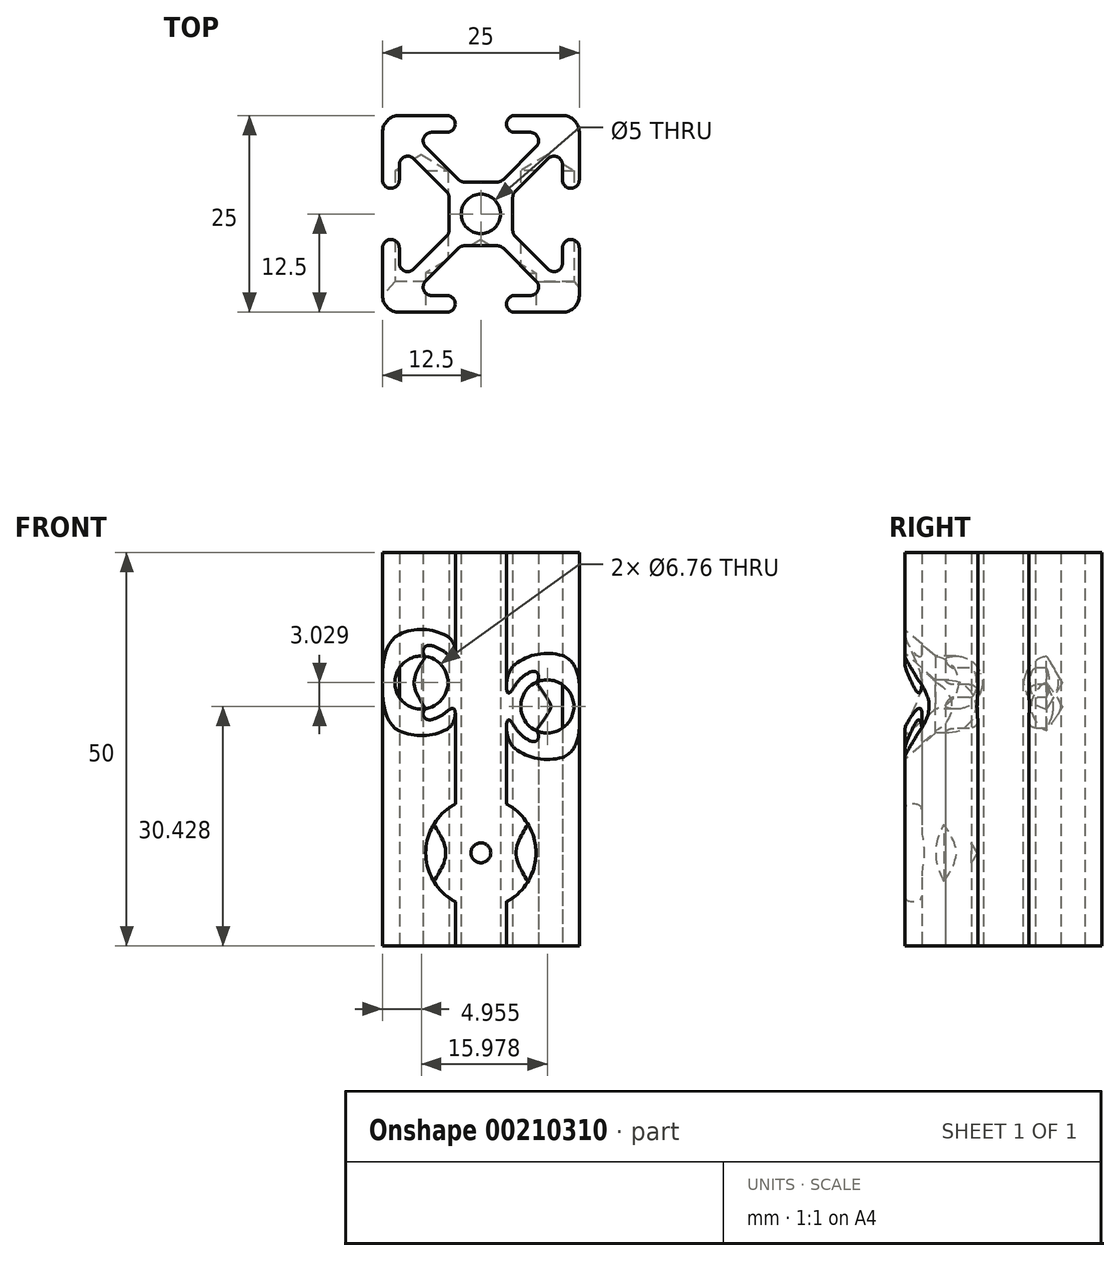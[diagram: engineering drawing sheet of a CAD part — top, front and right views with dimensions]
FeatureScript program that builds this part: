
annotation { "Feature Type Name" : "Feature", "Feature Type Description" : "" }
export const myFeature = defineFeature(function(context is Context, id is Id, definition is map)
    precondition{}
    {
        {
            var Q0;
            Q0=qCreatedBy(makeId("Top.planeOp"),FACE);
            var sketch = newSketch(context, id + "F0", { "sketchPlane" : qUnion([Q0])});
            skCircle(sketch, "E0", {"center": v(0, 0) * mm, "radius": 2.5 * mm});
            skLineSegment(sketch, "E1", {"start": v(0, 0) * mm, "end": v(0, 4.05) * mm, "construction": true});
            skLineSegment(sketch, "E2", {"start": v(0, 0) * mm, "end": v(-4.05, 0) * mm, "construction": true});
            skLineSegment(sketch, "E3", {"start": v(0, 0) * mm, "end": v(-12.5, 12.5) * mm, "construction": true});
            skLineSegment(sketch, "E4", {"start": v(-12.5, 10.36) * mm, "end": v(-12.5, 4.32) * mm});
            skLineSegment(sketch, "E5", {"start": v(-10.36, 12.5) * mm, "end": v(-4.32, 12.5) * mm});
            skLineSegment(sketch, "E6", {"start": v(-4.32, 10.36) * mm, "end": v(-6.26, 10.36) * mm});
            skLineSegment(sketch, "E7", {"start": v(-10.36, 6.26) * mm, "end": v(-10.36, 4.32) * mm});
            skArc(sketch, "E8", {"start": v(-4.32, 12.5) * mm, "mid": v(-3.25, 11.43) * mm, "end": v(-4.32, 10.36) * mm});
            skArc(sketch, "E9", {"start": v(-10.36, 4.32) * mm, "mid": v(-11.43, 3.25) * mm, "end": v(-12.5, 4.32) * mm});
            skLineSegment(sketch, "E10", {"start": v(0, 4.05) * mm, "end": v(-2.1, 4.05) * mm});
            skLineSegment(sketch, "E11", {"start": v(-4.05, 2.1) * mm, "end": v(-4.05, 0) * mm});
            skLineSegment(sketch, "E12", {"start": v(-8.53, 7.02) * mm, "end": v(-4.36, 2.85) * mm});
            skLineSegment(sketch, "E13", {"start": v(-7.02, 8.53) * mm, "end": v(-2.85, 4.36) * mm});
            skLineSegment(sketch, "E14.0.MirrorCS", {"start": v(10.36, 6.26) * mm, "end": v(10.36, 4.32) * mm});
            skLineSegment(sketch, "E14.1.MirrorCS", {"start": v(7.02, 8.53) * mm, "end": v(2.85, 4.36) * mm});
            skArc(sketch, "E14.2.MirrorCS", {"start": v(4.32, 12.5) * mm, "mid": v(3.25, 11.43) * mm, "end": v(4.32, 10.36) * mm});
            skArc(sketch, "E14.3.MirrorCS", {"start": v(10.36, 4.32) * mm, "mid": v(11.43, 3.25) * mm, "end": v(12.5, 4.32) * mm});
            skLineSegment(sketch, "E14.4.MirrorCS", {"start": v(10.36, 12.5) * mm, "end": v(4.32, 12.5) * mm});
            skLineSegment(sketch, "E14.5.MirrorCS", {"start": v(4.32, 10.36) * mm, "end": v(6.26, 10.36) * mm});
            skLineSegment(sketch, "E14.6.MirrorCS", {"start": v(12.5, 10.36) * mm, "end": v(12.5, 4.32) * mm});
            skLineSegment(sketch, "E14.7.MirrorCS", {"start": v(8.53, 7.02) * mm, "end": v(4.36, 2.85) * mm});
            skLineSegment(sketch, "E15.0.MirrorCS", {"start": v(0, 4.05) * mm, "end": v(2.1, 4.05) * mm});
            skLineSegment(sketch, "E16.0.MirrorCS", {"start": v(4.05, 2.1) * mm, "end": v(4.05, 0) * mm});
            skLineSegment(sketch, "E17.0.MirrorCS", {"start": v(10.36, -12.5) * mm, "end": v(4.32, -12.5) * mm});
            skLineSegment(sketch, "E17.1.MirrorCS", {"start": v(12.5, -10.36) * mm, "end": v(12.5, -4.32) * mm});
            skArc(sketch, "E17.2.MirrorCS", {"start": v(4.32, -12.5) * mm, "mid": v(3.25, -11.43) * mm, "end": v(4.32, -10.36) * mm});
            skLineSegment(sketch, "E17.3.MirrorCS", {"start": v(-7.02, -8.53) * mm, "end": v(-2.85, -4.36) * mm});
            skLineSegment(sketch, "E17.4.MirrorCS", {"start": v(7.02, -8.53) * mm, "end": v(2.85, -4.36) * mm});
            skLineSegment(sketch, "E17.5.MirrorCS", {"start": v(10.36, -6.26) * mm, "end": v(10.36, -4.32) * mm});
            skLineSegment(sketch, "E17.6.MirrorCS", {"start": v(8.53, -7.02) * mm, "end": v(4.36, -2.85) * mm});
            skLineSegment(sketch, "E17.7.MirrorCS", {"start": v(-10.36, -12.5) * mm, "end": v(-4.32, -12.5) * mm});
            skLineSegment(sketch, "E17.8.MirrorCS", {"start": v(-4.32, -10.36) * mm, "end": v(-6.26, -10.36) * mm});
            skLineSegment(sketch, "E17.9.MirrorCS", {"start": v(4.32, -10.36) * mm, "end": v(6.26, -10.36) * mm});
            skArc(sketch, "E17.10.MirrorCS", {"start": v(10.36, -4.32) * mm, "mid": v(11.43, -3.25) * mm, "end": v(12.5, -4.32) * mm});
            skLineSegment(sketch, "E17.11.MirrorCS", {"start": v(-12.5, -10.36) * mm, "end": v(-12.5, -4.32) * mm});
            skLineSegment(sketch, "E17.12.MirrorCS", {"start": v(0, -4.05) * mm, "end": v(2.1, -4.05) * mm});
            skArc(sketch, "E17.13.MirrorCS", {"start": v(-4.32, -12.5) * mm, "mid": v(-3.25, -11.43) * mm, "end": v(-4.32, -10.36) * mm});
            skLineSegment(sketch, "E17.14.MirrorCS", {"start": v(-8.53, -7.02) * mm, "end": v(-4.36, -2.85) * mm});
            skArc(sketch, "E17.15.MirrorCS", {"start": v(-10.36, -4.32) * mm, "mid": v(-11.43, -3.25) * mm, "end": v(-12.5, -4.32) * mm});
            skLineSegment(sketch, "E17.16.MirrorCS", {"start": v(-10.36, -6.26) * mm, "end": v(-10.36, -4.32) * mm});
            skLineSegment(sketch, "E17.17.MirrorCS", {"start": v(0, -4.05) * mm, "end": v(-2.1, -4.05) * mm});
            skLineSegment(sketch, "E18.0.MirrorCS", {"start": v(4.05, -2.1) * mm, "end": v(4.05, 0) * mm});
            skLineSegment(sketch, "E19.0.MirrorCS", {"start": v(-4.05, -2.1) * mm, "end": v(-4.05, 0) * mm});
            skPoint(sketch, "E20.visualSharp", {"position": v(-12.5, 12.5) * mm});
            skArc(sketch, "E20.filletArc", {"start": v(-10.36, 12.5) * mm, "mid": v(-11.87, 11.87) * mm, "end": v(-12.5, 10.36) * mm});
            skPoint(sketch, "E21.visualSharp", {"position": v(12.5, 12.5) * mm});
            skArc(sketch, "E21.filletArc", {"start": v(12.5, 10.36) * mm, "mid": v(11.87, 11.87) * mm, "end": v(10.36, 12.5) * mm});
            skPoint(sketch, "E22.visualSharp", {"position": v(12.5, -12.5) * mm});
            skArc(sketch, "E22.filletArc", {"start": v(10.36, -12.5) * mm, "mid": v(11.87, -11.87) * mm, "end": v(12.5, -10.36) * mm});
            skPoint(sketch, "E23.visualSharp", {"position": v(-12.5, -12.5) * mm});
            skArc(sketch, "E23.filletArc", {"start": v(-12.5, -10.36) * mm, "mid": v(-11.87, -11.87) * mm, "end": v(-10.36, -12.5) * mm});
            skPoint(sketch, "E24.visualSharp", {"position": v(4.05, 4.05) * mm});
            skPoint(sketch, "E25.visualSharp", {"position": v(-10.36, 8.85) * mm});
            skArc(sketch, "E25.filletArc", {"start": v(-8.53, 7.02) * mm, "mid": v(-9.7, 7.25) * mm, "end": v(-10.36, 6.26) * mm});
            skPoint(sketch, "E26.visualSharp", {"position": v(-8.85, 10.36) * mm});
            skArc(sketch, "E26.filletArc", {"start": v(-6.26, 10.36) * mm, "mid": v(-7.25, 9.7) * mm, "end": v(-7.02, 8.53) * mm});
            skPoint(sketch, "E27.visualSharp", {"position": v(8.85, 10.36) * mm});
            skArc(sketch, "E27.filletArc", {"start": v(7.02, 8.53) * mm, "mid": v(7.25, 9.7) * mm, "end": v(6.26, 10.36) * mm});
            skPoint(sketch, "E28.visualSharp", {"position": v(10.36, 8.85) * mm});
            skArc(sketch, "E28.filletArc", {"start": v(10.36, 6.26) * mm, "mid": v(9.7, 7.25) * mm, "end": v(8.53, 7.02) * mm});
            skPoint(sketch, "E29.visualSharp", {"position": v(10.36, -8.85) * mm});
            skArc(sketch, "E29.filletArc", {"start": v(8.53, -7.02) * mm, "mid": v(9.7, -7.25) * mm, "end": v(10.36, -6.26) * mm});
            skPoint(sketch, "E30.visualSharp", {"position": v(8.85, -10.36) * mm});
            skArc(sketch, "E30.filletArc", {"start": v(6.26, -10.36) * mm, "mid": v(7.25, -9.7) * mm, "end": v(7.02, -8.53) * mm});
            skPoint(sketch, "E31.visualSharp", {"position": v(-8.85, -10.36) * mm});
            skArc(sketch, "E31.filletArc", {"start": v(-7.02, -8.53) * mm, "mid": v(-7.25, -9.7) * mm, "end": v(-6.26, -10.36) * mm});
            skPoint(sketch, "E32.visualSharp", {"position": v(-10.36, -8.85) * mm});
            skArc(sketch, "E32.filletArc", {"start": v(-10.36, -6.26) * mm, "mid": v(-9.7, -7.25) * mm, "end": v(-8.53, -7.02) * mm});
            skPoint(sketch, "E33.orphan", {"position": v(-4.05, 4.05) * mm});
            skPoint(sketch, "E34.orphan", {"position": v(4.05, -4.05) * mm});
            skPoint(sketch, "E35.orphan", {"position": v(-4.05, -4.05) * mm});
            skPoint(sketch, "E36.visualSharp", {"position": v(-2.54, 4.05) * mm});
            skArc(sketch, "E36.filletArc", {"start": v(-2.85, 4.36) * mm, "mid": v(-2.5, 4.13) * mm, "end": v(-2.1, 4.05) * mm});
            skPoint(sketch, "E37.visualSharp", {"position": v(2.54, 4.05) * mm});
            skArc(sketch, "E37.filletArc", {"start": v(2.1, 4.05) * mm, "mid": v(2.5, 4.13) * mm, "end": v(2.85, 4.36) * mm});
            skPoint(sketch, "E38.visualSharp", {"position": v(-4.05, 2.54) * mm});
            skArc(sketch, "E38.filletArc", {"start": v(-4.05, 2.1) * mm, "mid": v(-4.13, 2.5) * mm, "end": v(-4.36, 2.85) * mm});
            skPoint(sketch, "E39.visualSharp", {"position": v(-4.05, -2.54) * mm});
            skArc(sketch, "E39.filletArc", {"start": v(-4.36, -2.85) * mm, "mid": v(-4.13, -2.5) * mm, "end": v(-4.05, -2.1) * mm});
            skPoint(sketch, "E40.visualSharp", {"position": v(-2.54, -4.05) * mm});
            skArc(sketch, "E40.filletArc", {"start": v(-2.1, -4.05) * mm, "mid": v(-2.5, -4.13) * mm, "end": v(-2.85, -4.36) * mm});
            skPoint(sketch, "E41.visualSharp", {"position": v(2.54, -4.05) * mm});
            skArc(sketch, "E41.filletArc", {"start": v(2.85, -4.36) * mm, "mid": v(2.5, -4.13) * mm, "end": v(2.1, -4.05) * mm});
            skPoint(sketch, "E42.visualSharp", {"position": v(4.05, -2.54) * mm});
            skArc(sketch, "E42.filletArc", {"start": v(4.05, -2.1) * mm, "mid": v(4.13, -2.5) * mm, "end": v(4.36, -2.85) * mm});
            skPoint(sketch, "E43.visualSharp", {"position": v(4.05, 2.54) * mm});
            skArc(sketch, "E43.filletArc", {"start": v(4.36, 2.85) * mm, "mid": v(4.13, 2.5) * mm, "end": v(4.05, 2.1) * mm});
            skSolve(sketch);
        }
        {
            var Q0;
            Q0=makeQuery(id+"F0.imprint","IMPRINT",FACE,{"disambiguationData":[TD([[makeQuery(id+"F0.imprint","IMPRINT",EDGE,{"derivedFrom":sQuery(id+"F0.wireOp",EDGE,"E0")}),-1.0]])]});
            extrude(context, id + "F1", {"entities" : qUnion([Q0]), "depth" : 50 * mm});
        }
        {
            var Q0;
            Q0=makeQuery(id+"F1.opExtrude","SWEPT_FACE",FACE,{"disambiguationData":[OSD([sQuery(id+"F0.wireOp",EDGE,"E17.7.MirrorCS")])]});
            var sketch = newSketch(context, id + "F2", { "sketchPlane" : qUnion([Q0])});
            skPoint(sketch, "E44", {"position": v(8.43, 30.43) * mm});
            skPoint(sketch, "E45", {"position": v(-7.55, 33.46) * mm});
            skSolve(sketch);
        }
        {
            var Q0;
            Q0=sQuery(id+"F2.wireOp",VERTEX,"E45");
            var Q1;
            Q1=sQuery(id+"F2.wireOp",VERTEX,"E44");
            var Q2;
            Q2=makeQuery(id+"F1.opExtrude","SWEPT_BODY",BODY,{"disambiguationData":[OSD([sQuery(id+"F0.wireOp",EDGE,"E0"),sQuery(id+"F0.wireOp",EDGE,"E4"),sQuery(id+"F0.wireOp",EDGE,"E5"),sQuery(id+"F0.wireOp",EDGE,"E6"),sQuery(id+"F0.wireOp",EDGE,"E7"),sQuery(id+"F0.wireOp",EDGE,"E8"),sQuery(id+"F0.wireOp",EDGE,"E9"),sQuery(id+"F0.wireOp",EDGE,"E11"),sQuery(id+"F0.wireOp",EDGE,"E12"),sQuery(id+"F0.wireOp",EDGE,"E13"),sQuery(id+"F0.wireOp",EDGE,"E14.0.MirrorCS"),sQuery(id+"F0.wireOp",EDGE,"E14.1.MirrorCS"),sQuery(id+"F0.wireOp",EDGE,"E14.2.MirrorCS"),sQuery(id+"F0.wireOp",EDGE,"E14.3.MirrorCS"),sQuery(id+"F0.wireOp",EDGE,"E14.4.MirrorCS"),sQuery(id+"F0.wireOp",EDGE,"E14.5.MirrorCS"),sQuery(id+"F0.wireOp",EDGE,"E14.6.MirrorCS"),sQuery(id+"F0.wireOp",EDGE,"E14.7.MirrorCS"),sQuery(id+"F0.wireOp",EDGE,"E15.0.MirrorCS"),sQuery(id+"F0.wireOp",EDGE,"E17.0.MirrorCS"),sQuery(id+"F0.wireOp",EDGE,"E17.1.MirrorCS"),sQuery(id+"F0.wireOp",EDGE,"E17.2.MirrorCS"),sQuery(id+"F0.wireOp",EDGE,"E17.3.MirrorCS"),sQuery(id+"F0.wireOp",EDGE,"E17.4.MirrorCS"),sQuery(id+"F0.wireOp",EDGE,"E17.5.MirrorCS"),sQuery(id+"F0.wireOp",EDGE,"E17.6.MirrorCS"),sQuery(id+"F0.wireOp",EDGE,"E17.7.MirrorCS"),sQuery(id+"F0.wireOp",EDGE,"E17.8.MirrorCS"),sQuery(id+"F0.wireOp",EDGE,"E17.9.MirrorCS"),sQuery(id+"F0.wireOp",EDGE,"E17.10.MirrorCS"),sQuery(id+"F0.wireOp",EDGE,"E17.11.MirrorCS"),sQuery(id+"F0.wireOp",EDGE,"E17.13.MirrorCS"),sQuery(id+"F0.wireOp",EDGE,"E17.14.MirrorCS"),sQuery(id+"F0.wireOp",EDGE,"E17.15.MirrorCS"),sQuery(id+"F0.wireOp",EDGE,"E17.16.MirrorCS"),sQuery(id+"F0.wireOp",EDGE,"E17.17.MirrorCS"),sQuery(id+"F0.wireOp",EDGE,"E18.0.MirrorCS"),sQuery(id+"F0.wireOp",EDGE,"E20.filletArc"),sQuery(id+"F0.wireOp",EDGE,"E21.filletArc"),sQuery(id+"F0.wireOp",EDGE,"E22.filletArc"),sQuery(id+"F0.wireOp",EDGE,"E23.filletArc"),sQuery(id+"F0.wireOp",EDGE,"E25.filletArc"),sQuery(id+"F0.wireOp",EDGE,"E26.filletArc"),sQuery(id+"F0.wireOp",EDGE,"E27.filletArc"),sQuery(id+"F0.wireOp",EDGE,"E28.filletArc"),sQuery(id+"F0.wireOp",EDGE,"E29.filletArc"),sQuery(id+"F0.wireOp",EDGE,"E30.filletArc"),sQuery(id+"F0.wireOp",EDGE,"E31.filletArc"),sQuery(id+"F0.wireOp",EDGE,"E32.filletArc"),sQuery(id+"F0.wireOp",EDGE,"E36.filletArc"),sQuery(id+"F0.wireOp",EDGE,"E37.filletArc"),sQuery(id+"F0.wireOp",EDGE,"E38.filletArc"),sQuery(id+"F0.wireOp",EDGE,"E39.filletArc"),sQuery(id+"F0.wireOp",EDGE,"E40.filletArc"),sQuery(id+"F0.wireOp",EDGE,"E41.filletArc"),sQuery(id+"F0.wireOp",EDGE,"E42.filletArc"),sQuery(id+"F0.wireOp",EDGE,"E43.filletArc")])]});
            hole(context, id + "F3", {"style" : HoleStyle.C_SINK, "endStyle" : HoleEndStyle.BLIND, "standardTappedOrClearance" : lookupTablePath({ "standard" : "ANSI", "fit" : "Normal (ASME)", "size" : "1/4", "type" : "Clearance" }), "standardBlindInLast" : lookupTablePath({ "fit" : "Free", "standard" : "ANSI", "size" : "1/4", "type" : "Clearance" }), "holeDiameter" : 6.76 * mm, "cSinkDiameter" : 13.5 * mm, "cSinkAngle" : 82 * degree, "holeDepth" : 18 * mm, "locations" : qUnion([Q0, Q1]), "scope" : qUnion([Q2])});
        }
        {
            var Q0;
            Q0=makeQuery(id+"F1.opExtrude","SWEPT_FACE",FACE,{"disambiguationData":[OSD([sQuery(id+"F0.wireOp",EDGE,"E17.0.MirrorCS")])]});
            var sketch = newSketch(context, id + "F4", { "sketchPlane" : qUnion([Q0])});
            skPoint(sketch, "E46", {"position": v(0, 11.83) * mm});
            skSolve(sketch);
        }
        {
            var Q0;
            Q0=sQuery(id+"F4.wireOp",VERTEX,"E46");
            var Q1;
            Q1=makeQuery(id+"F1.opExtrude","SWEPT_BODY",BODY,{"disambiguationData":[OSD([sQuery(id+"F0.wireOp",EDGE,"E0"),sQuery(id+"F0.wireOp",EDGE,"E4"),sQuery(id+"F0.wireOp",EDGE,"E5"),sQuery(id+"F0.wireOp",EDGE,"E6"),sQuery(id+"F0.wireOp",EDGE,"E7"),sQuery(id+"F0.wireOp",EDGE,"E8"),sQuery(id+"F0.wireOp",EDGE,"E9"),sQuery(id+"F0.wireOp",EDGE,"E11"),sQuery(id+"F0.wireOp",EDGE,"E12"),sQuery(id+"F0.wireOp",EDGE,"E13"),sQuery(id+"F0.wireOp",EDGE,"E14.0.MirrorCS"),sQuery(id+"F0.wireOp",EDGE,"E14.1.MirrorCS"),sQuery(id+"F0.wireOp",EDGE,"E14.2.MirrorCS"),sQuery(id+"F0.wireOp",EDGE,"E14.3.MirrorCS"),sQuery(id+"F0.wireOp",EDGE,"E14.4.MirrorCS"),sQuery(id+"F0.wireOp",EDGE,"E14.5.MirrorCS"),sQuery(id+"F0.wireOp",EDGE,"E14.6.MirrorCS"),sQuery(id+"F0.wireOp",EDGE,"E14.7.MirrorCS"),sQuery(id+"F0.wireOp",EDGE,"E15.0.MirrorCS"),sQuery(id+"F0.wireOp",EDGE,"E17.0.MirrorCS"),sQuery(id+"F0.wireOp",EDGE,"E17.1.MirrorCS"),sQuery(id+"F0.wireOp",EDGE,"E17.2.MirrorCS"),sQuery(id+"F0.wireOp",EDGE,"E17.3.MirrorCS"),sQuery(id+"F0.wireOp",EDGE,"E17.4.MirrorCS"),sQuery(id+"F0.wireOp",EDGE,"E17.5.MirrorCS"),sQuery(id+"F0.wireOp",EDGE,"E17.6.MirrorCS"),sQuery(id+"F0.wireOp",EDGE,"E17.7.MirrorCS"),sQuery(id+"F0.wireOp",EDGE,"E17.8.MirrorCS"),sQuery(id+"F0.wireOp",EDGE,"E17.9.MirrorCS"),sQuery(id+"F0.wireOp",EDGE,"E17.10.MirrorCS"),sQuery(id+"F0.wireOp",EDGE,"E17.11.MirrorCS"),sQuery(id+"F0.wireOp",EDGE,"E17.13.MirrorCS"),sQuery(id+"F0.wireOp",EDGE,"E17.14.MirrorCS"),sQuery(id+"F0.wireOp",EDGE,"E17.15.MirrorCS"),sQuery(id+"F0.wireOp",EDGE,"E17.16.MirrorCS"),sQuery(id+"F0.wireOp",EDGE,"E17.17.MirrorCS"),sQuery(id+"F0.wireOp",EDGE,"E18.0.MirrorCS"),sQuery(id+"F0.wireOp",EDGE,"E20.filletArc"),sQuery(id+"F0.wireOp",EDGE,"E21.filletArc"),sQuery(id+"F0.wireOp",EDGE,"E22.filletArc"),sQuery(id+"F0.wireOp",EDGE,"E23.filletArc"),sQuery(id+"F0.wireOp",EDGE,"E25.filletArc"),sQuery(id+"F0.wireOp",EDGE,"E26.filletArc"),sQuery(id+"F0.wireOp",EDGE,"E27.filletArc"),sQuery(id+"F0.wireOp",EDGE,"E28.filletArc"),sQuery(id+"F0.wireOp",EDGE,"E29.filletArc"),sQuery(id+"F0.wireOp",EDGE,"E30.filletArc"),sQuery(id+"F0.wireOp",EDGE,"E31.filletArc"),sQuery(id+"F0.wireOp",EDGE,"E32.filletArc"),sQuery(id+"F0.wireOp",EDGE,"E36.filletArc"),sQuery(id+"F0.wireOp",EDGE,"E37.filletArc"),sQuery(id+"F0.wireOp",EDGE,"E38.filletArc"),sQuery(id+"F0.wireOp",EDGE,"E39.filletArc"),sQuery(id+"F0.wireOp",EDGE,"E40.filletArc"),sQuery(id+"F0.wireOp",EDGE,"E41.filletArc"),sQuery(id+"F0.wireOp",EDGE,"E42.filletArc"),sQuery(id+"F0.wireOp",EDGE,"E43.filletArc")])]});
            hole(context, id + "F5", {"style" : HoleStyle.SIMPLE, "endStyle" : HoleEndStyle.BLIND, "holeDiameter" : 14 * mm, "holeDepth" : 5 * mm, "locations" : qUnion([Q0]), "scope" : qUnion([Q1])});
        }
    });
